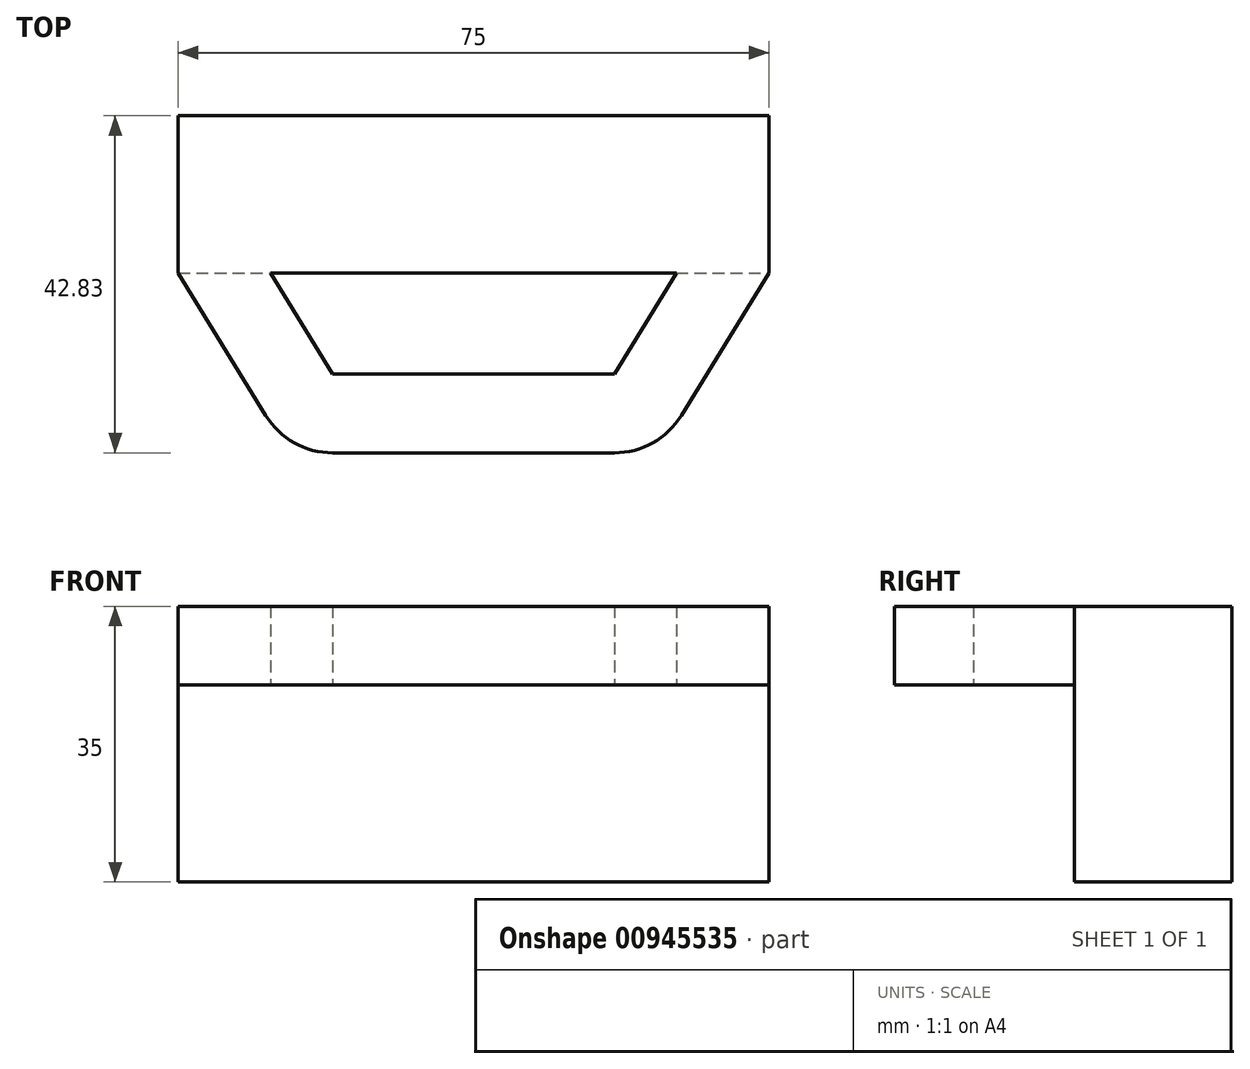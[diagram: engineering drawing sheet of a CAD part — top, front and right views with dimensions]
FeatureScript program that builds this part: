
annotation { "Feature Type Name" : "Feature", "Feature Type Description" : "" }
export const myFeature = defineFeature(function(context is Context, id is Id, definition is map)
    precondition{}
    {
        {
            var Q0;
            Q0=qCreatedBy(makeId("Top.planeOp"),FACE);
            var sketch = newSketch(context, id + "F0", { "sketchPlane" : qUnion([Q0])});
            skLineSegment(sketch, "E0.bottom", {"start": v(0, 0) * mm, "end": v(75, 0) * mm});
            skLineSegment(sketch, "E0.top", {"start": v(0, 20) * mm, "end": v(75, 20) * mm});
            skLineSegment(sketch, "E0.left", {"start": v(0, 0) * mm, "end": v(0, 20) * mm});
            skLineSegment(sketch, "E0.right", {"start": v(75, 0) * mm, "end": v(75, 20) * mm});
            skLineSegment(sketch, "E1", {"start": v(0, 0) * mm, "end": v(11.1, -18.07) * mm});
            skLineSegment(sketch, "E2", {"start": v(19.62, -22.83) * mm, "end": v(55.38, -22.83) * mm});
            skLineSegment(sketch, "E3", {"start": v(63.9, -18.07) * mm, "end": v(75, 0) * mm});
            skLineSegment(sketch, "E4", {"start": v(37.5, -22.83) * mm, "end": v(37.5, 0) * mm});
            skPoint(sketch, "E5.visualSharp", {"position": v(14.03, -22.83) * mm});
            skArc(sketch, "E5.filletArc", {"start": v(11.1, -18.07) * mm, "mid": v(14.74, -21.56) * mm, "end": v(19.62, -22.83) * mm});
            skPoint(sketch, "E6.visualSharp", {"position": v(60.97, -22.83) * mm});
            skArc(sketch, "E6.filletArc", {"start": v(55.38, -22.83) * mm, "mid": v(60.26, -21.56) * mm, "end": v(63.9, -18.07) * mm});
            skLineSegment(sketch, "E7.0", {"start": v(55.38, -12.83) * mm, "end": v(63.26, 0) * mm});
            skLineSegment(sketch, "E7.1", {"start": v(19.62, -12.83) * mm, "end": v(55.38, -12.83) * mm});
            skLineSegment(sketch, "E7.2", {"start": v(11.74, 0) * mm, "end": v(19.62, -12.83) * mm});
            skSolve(sketch);
        }
        {
            var Q0;
            Q0=makeQuery(id+"F0.imprint","IMPRINT",FACE,{"disambiguationData":[TD([[makeQuery(id+"F0.imprint","IMPRINT",EDGE,{"derivedFrom":sQuery(id+"F0.wireOp",EDGE,"E0.top")}),-1.0]])]});
            extrude(context, id + "F1", {"entities" : qUnion([Q0]), "oppositeDirection" : true, "depth" : 25 * mm, "offsetDistance" : 25 * mm});
        }
        {
            var Q0;
            Q0 = qSketchRegion(id + "F0", true);
            extrude(context, id + "F2", {"entities" : qUnion([Q0]), "operationType" : NewBodyOperationType.ADD, "depth" : 10 * mm, "offsetDistance" : 25 * mm});
        }
    });
